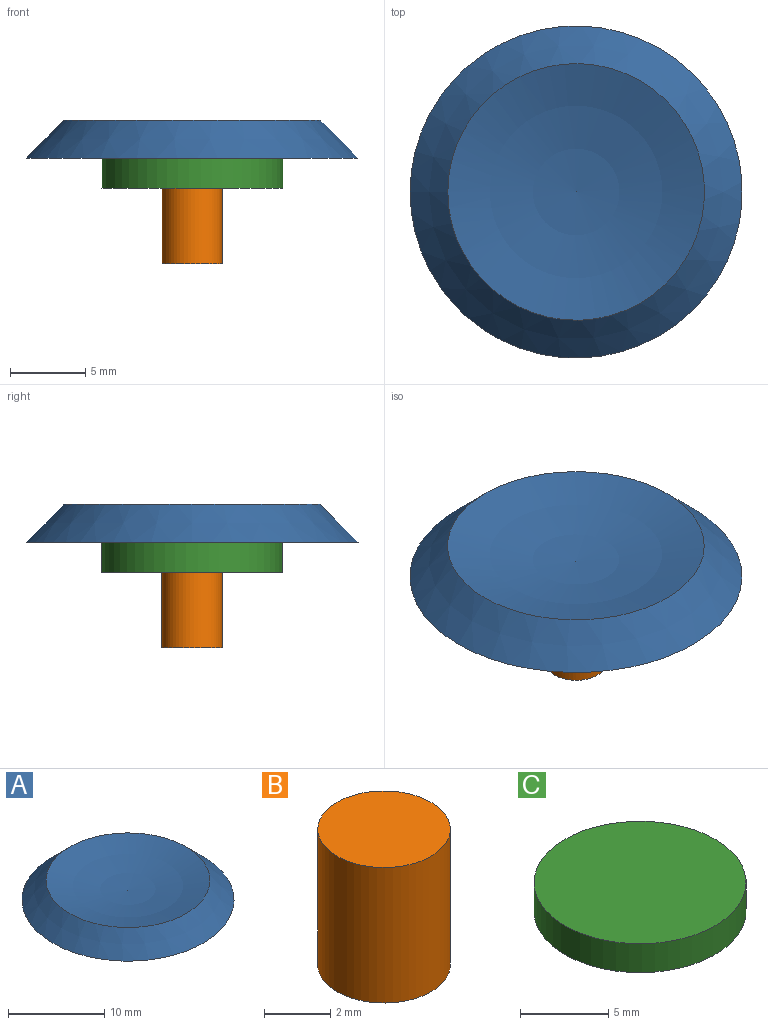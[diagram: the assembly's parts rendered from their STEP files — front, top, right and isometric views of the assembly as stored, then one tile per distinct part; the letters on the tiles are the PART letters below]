
ASSEMBLY  parts=3 mates=2
PART A: 3 faces, bbox 22x22x2.5 mm
  f0: plane 22x22mm, normal (0,0,-1), area 380.1mm2, adj f1
  f1: cone r=11mm half-angle=45deg, axis (0,0,-1), area 216.6mm2, adj f0,f2
  f2: sphere r=29.52mm, area 231.9mm2, adj f1
PART B: 3 faces, bbox 4x4x5 mm
  f0: cylinder r=2mm len=5mm, axis (0,0,-1), area 62.8mm2, adj f1,f2
  f1: plane 4x4mm, normal (0,0,1), area 12.6mm2, adj f0
  f2: plane 4x4mm, normal (0,0,-1), area 12.6mm2, adj f0
PART C: 3 faces, bbox 12x12x2 mm
  f0: cylinder r=6mm len=12mm, axis (0,0,-1), area 75.4mm2, adj f1,f2
  f1: plane 12x12mm, normal (0,0,1), area 113.1mm2, adj f0
  f2: plane 12x12mm, normal (0,0,-1), area 113.1mm2, adj f0
PLACE A t=(-6.02,-1.13,1.77)mm
PLACE B t=(57.36,-24.04,-5.23)mm
PLACE C t=(45.46,-39.8,-0.23)mm
MATE fastened B.f0 <-> C.f0  axis (0,0,1) through (-6.02,-1.13,-0.23)mm
MATE fastened C.f0 <-> A.f1  axis (0,0,1) through (-6.02,-1.13,1.77)mm
